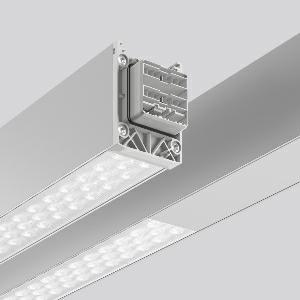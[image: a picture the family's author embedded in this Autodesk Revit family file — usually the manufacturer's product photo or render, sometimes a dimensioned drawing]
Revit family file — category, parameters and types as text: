
# Revit family: linedo_4_5m_30_11001100_954530_840_776_504_becd
name_source: partatom
category: Lighting Fixtures
units: mm (PartAtom-declared; Revit-internal decimal feet)

## family parameters
Cut with Voids When Loaded = No
Host = Face
Light Source = No
Part Type = Normal
Room Calculation Point = No
Round Connector Dimension = Use Diameter
Shared = No

## types (1)
- LINEDO_4,5m_30_11001100 (1 x LED Modul 840, 5225 lm, 4000)
    Apparent Load = 137 VA
    CIE Flux Codes = 89 97 99 100 100
    Color Rendering = 80
    Color Temperature = 4000
    Default Elevation = 1800 mm
    Description = LINEDO, 137 W, 20900 lm, 840, aluminium, DALI
Continuous line luminaire, L 4547 B 58 H 76
    Height = 76 mm
    Lamp = 1 x LED Modul 840
    Lamp Light Flux = 5225 lm
    Lamp count = 1
    Length = 4547 mm
    Lifetime = 50000 h
    Luminous efficacy = 153 lm/W
    Manufacturer = RZB
    ModVariant = No
    Model = 954530.840.776.504
    Mounting Place = Ceiling
    Mounting Type = Surface mounted, Pendant
    Number of Poles = 1
    OnlyDefault = Yes
    Power Factor = 1
    Product Name = LINEDO_4,5m_30_11001100
    Product group = Surface mounted continuous line luminaire system
    ProductGroupID = 310
    Protection Class = Protection class I
    Protection Degree = IP 54
    RLX_Detail_Level = 1
    RLX_Emergency_Light_Flux = 0 lm
    RLX_Emergency_Type = 0
    RLX_Emergency_Type_DB = No
    RlxData = <blob elided: 52565 chars, md5=b36ef9e1>
    Socket = socket
    Standby Power = 0 W
    System Light Flux = 20900 lm
    System Power = 137 W
    Type Comments = Product without accessories
    Type Image = 954530.850.476.504.jpg
    URL = http://relux.com
    VarID = ---
    Voltage = 230 V
    Voltage Range = 220-240 V
    Weight = 0.00 kg
    Width = 58 mm

## geometry (parser evidence)
native form markers: Blend x4, Sweep x19
no freeform markers — native parametric forms only
